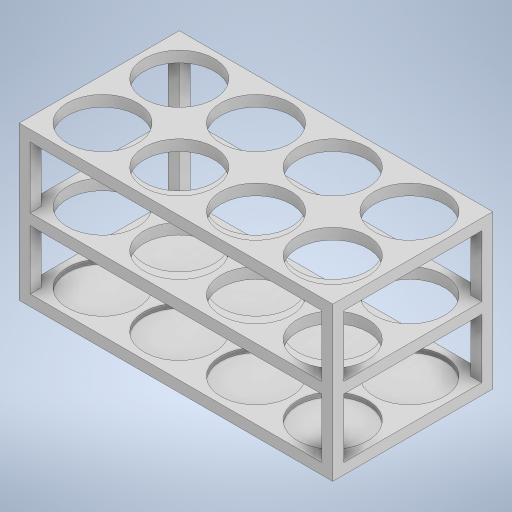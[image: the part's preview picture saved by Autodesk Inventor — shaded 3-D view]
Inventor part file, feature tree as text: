
AUTODESK INVENTOR PART (.ipt)
format: ipt  version: 2023.5 (Build 275446000, 446)  size: 412,160 bytes
history: native  units: in
note: dims shown in document units (in); Inventor stores cm internally (conversion verified against a paired STEP export)
features: extrude x4, sketch x4
ambient origin geometry x8: Origin, YZ Plane, XZ Plane, XY Plane, X Axis, Y Axis, Z Axis, Center Point
bodies: Solid1 (feature_tree)
feature tree (8):
  extrude  "Extrusion1"  Depth=1.2598in
  extrude  "Extrusion2"  Depth=1.2598in
  extrude  "Extrusion3"  Depth=1.2598in
  extrude  "Extrusion4"  Depth=1.2598in
  sketch  "Sketch1"  dims[d10=0.1181in d12=1.2598in]
  sketch  "Sketch3"  dims[d13=1.2598in d14=1.2598in]
  sketch  "Sketch4"  dims[d15=1.2598in d16=1.2598in]
  sketch  "Sketch5"  dims[d17=1.2598in d18=1.2598in d19=1.2598in d20=1.378in d21=0.748in d22=1.378in d23=1.378in d24=0.748in d25=0.748in d26=0.748in d27=0.748in d28=0.748in d29=0.748in d30=1.378in d31=1.378in d32=1.378in d33=1.378in d34=0.748in d35=2.7559in d36=0.0in d37=0.1969in d38=0.1969in d39=0.1969in d43=2.7559in d44=0.0in d45=0.1969in d46=0.1969in d47=0.1969in d49=0.1969in d50=0.1969in d51=0.1969in d53=0.0in d54=0.0in d55=0.1181in d56=0.0in d57=0.1969in d58=0.1969in d59=0.1969in d62=0.1969in d63=0.1969in]
